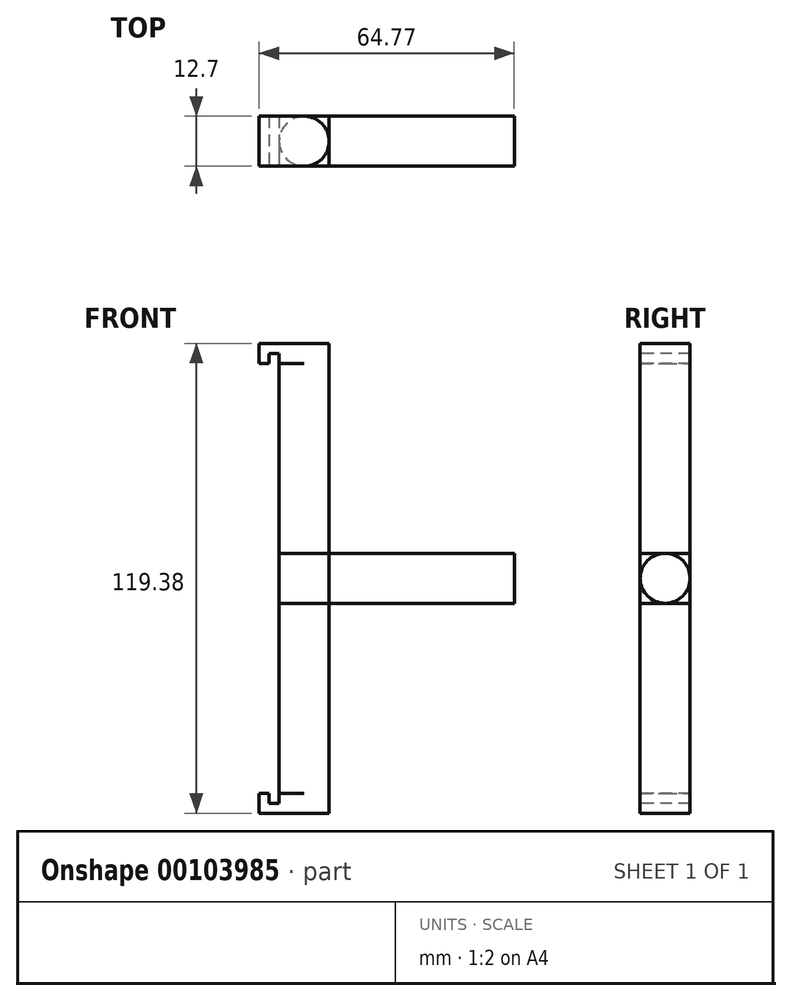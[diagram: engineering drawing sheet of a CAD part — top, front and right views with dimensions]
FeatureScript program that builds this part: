
annotation { "Feature Type Name" : "Feature", "Feature Type Description" : "" }
export const myFeature = defineFeature(function(context is Context, id is Id, definition is map)
    precondition{}
    {
        {
            var Q0;
            Q0=qCreatedBy(makeId("Right.planeOp"),FACE);
            var sketch = newSketch(context, id + "F0", { "sketchPlane" : qUnion([Q0])});
            skCircle(sketch, "E0", {"center": v(42.26, 52.7) * mm, "radius": 6.35 * mm});
            skSolve(sketch);
        }
        {
            var Q0;
            Q0=qSketchRegion(id+"F0",true);
            extrude(context, id + "F1", {"entities" : qUnion([Q0]), "depth" : 47 * mm});
        }
        {
            var Q0;
            Q0=makeQuery(id+"F1.opExtrude","CAP_FACE",FACE,{"disambiguationData":[OSD([sQuery(id+"F0.wireOp",EDGE,"E0")])],"isStart":true});
            var sketch = newSketch(context, id + "F2", { "sketchPlane" : qUnion([Q0])});
            skLineSegment(sketch, "E1", {"start": v(-42.26, 52.7) * mm, "end": v(-48.6, 52.7) * mm, "construction": true});
            skLineSegment(sketch, "E2", {"start": v(-42.26, 52.7) * mm, "end": v(-42.26, 59.04) * mm, "construction": true});
            skLineSegment(sketch, "E3.top", {"start": v(-48.6, 46.34) * mm, "end": v(-35.9, 46.34) * mm});
            skLineSegment(sketch, "E3.left", {"start": v(-48.6, 59.04) * mm, "end": v(-48.6, 46.34) * mm});
            skLineSegment(sketch, "E3.right", {"start": v(-35.9, 59.04) * mm, "end": v(-35.9, 46.34) * mm});
            skPoint(sketch, "E3.middle", {"position": v(-42.26, 52.7) * mm});
            skLineSegment(sketch, "E4", {"start": v(-35.9, 52.7) * mm, "end": v(-48.6, 52.7) * mm});
            skSolve(sketch);
        }
        {
            var Q0;
            {var subQ0=sQuery(id+"F2.wireOp",EDGE,"E3.left");var subQ1=sQuery(id+"F2.wireOp",EDGE,"E3.bottom");var subQ2=makeQuery(id+"F2.imprint","INTERSECT",VERTEX,{"derivedFrom":[subQ1,subQ0]});Q0=makeQuery(id+"F2.imprint","IMPRINT",FACE,{"disambiguationData":[TD([[makeQuery(id+"F2.imprint","IMPRINT",EDGE,{"disambiguationData":[TD([[subQ2,-1.0]])],"derivedFrom":subQ1}),-1.0]])]});}
            var Q1;
            {var subQ0=sQuery(id+"F2.wireOp",EDGE,"E3.right");var subQ1=sQuery(id+"F2.wireOp",EDGE,"E3.bottom");var subQ2=makeQuery(id+"F2.imprint","INTERSECT",VERTEX,{"derivedFrom":[subQ1,subQ0]});Q1=makeQuery(id+"F2.imprint","IMPRINT",FACE,{"disambiguationData":[TD([[makeQuery(id+"F2.imprint","IMPRINT",EDGE,{"disambiguationData":[TD([[subQ2,1.0]])],"derivedFrom":subQ1}),-1.0]])]});}
            var Q2;
            {var subQ0=makeQuery(id+"F1.opExtrude","CAP_EDGE",EDGE,{"disambiguationData":[OSD([sQuery(id+"F0.wireOp",EDGE,"E0")])],"isStart":true});var subQ1=makeQuery(id+"F2.imprint","INTERSECT",VERTEX,{"derivedFrom":[subQ0,sQuery(id+"F2.wireOp",EDGE,"E3.bottom")]});Q2=makeQuery(id+"F2.imprint","IMPRINT",FACE,{"disambiguationData":[TD([[makeQuery(id+"F2.imprint","IMPRINT",EDGE,{"disambiguationData":[TD([[subQ1,1.0]])],"derivedFrom":subQ0}),-1.0]])]});}
            var Q3;
            {var subQ0=sQuery(id+"F2.wireOp",EDGE,"E3.left");var subQ1=sQuery(id+"F2.wireOp",EDGE,"E3.top");var subQ2=makeQuery(id+"F2.imprint","INTERSECT",VERTEX,{"derivedFrom":[subQ1,subQ0]});Q3=makeQuery(id+"F2.imprint","IMPRINT",FACE,{"disambiguationData":[TD([[makeQuery(id+"F2.imprint","IMPRINT",EDGE,{"disambiguationData":[TD([[subQ2,-1.0]])],"derivedFrom":subQ1}),1.0]])]});}
            var Q4;
            {var subQ0=sQuery(id+"F2.wireOp",EDGE,"E3.right");var subQ1=sQuery(id+"F2.wireOp",EDGE,"E3.top");var subQ2=makeQuery(id+"F2.imprint","INTERSECT",VERTEX,{"derivedFrom":[subQ1,subQ0]});Q4=makeQuery(id+"F2.imprint","IMPRINT",FACE,{"disambiguationData":[TD([[makeQuery(id+"F2.imprint","IMPRINT",EDGE,{"disambiguationData":[TD([[subQ2,1.0]])],"derivedFrom":subQ1}),1.0]])]});}
            extrude(context, id + "F3", {"entities" : qUnion([Q0, Q1, Q2, Q3, Q4]), "operationType" : NewBodyOperationType.ADD, "depth" : 12.7 * mm});
        }
        {
            var Q0;
            Q0=makeQuery(id+"F3.opExtrude","SWEPT_FACE",FACE,{"disambiguationData":[OSD([sQuery(id+"F2.wireOp",EDGE,"E3.top")])]});
            var sketch = newSketch(context, id + "F4", { "sketchPlane" : qUnion([Q0])});
            skCircle(sketch, "E5", {"center": v(-6.35, -42.26) * mm, "radius": 6.35 * mm});
            skPoint(sketch, "E5.centerSnap0", {"position": v(-6.35, -48.6) * mm});
            skPoint(sketch, "E5.centerSnap1", {"position": v(-12.7, -42.26) * mm});
            skSolve(sketch);
        }
        {
            var Q0;
            {var subQ0=sQuery(id+"F4.wireOp",EDGE,"E5");var subQ4=sQuery(id+"F2.wireOp",EDGE,"E3.top");var subQ10=makeQuery(id+"F4.imprint","INTERSECT",VERTEX,{"derivedFrom":[makeQuery(id+"F3.opExtrude","CAP_EDGE",EDGE,{"disambiguationData":[OSD([subQ4])],"isStart":false}),subQ0]});Q0=makeQuery(id+"F4.imprint","IMPRINT",FACE,{"disambiguationData":[TD([[makeQuery(id+"F4.imprint","IMPRINT",EDGE,{"disambiguationData":[TD([[subQ10,1.0]])],"derivedFrom":subQ0}),1.0]])]});}
            extrude(context, id + "F5", {"entities" : qUnion([Q0]), "operationType" : NewBodyOperationType.ADD, "depth" : 50.8 * mm});
        }
        {
            var Q0;
            Q0=makeQuery(id+"F5.opExtrude","CAP_FACE",FACE,{"disambiguationData":[OSD([sQuery(id+"F4.wireOp",EDGE,"E5")])],"isStart":false});
            var sketch = newSketch(context, id + "F6", { "sketchPlane" : qUnion([Q0])});
            skLineSegment(sketch, "E6", {"start": v(-6.35, -42.26) * mm, "end": v(-6.35, -48.6) * mm});
            skLineSegment(sketch, "E7", {"start": v(-6.35, -42.26) * mm, "end": v(-12.7, -42.26) * mm});
            skLineSegment(sketch, "E8", {"start": v(-6.35, -48.6) * mm, "end": v(-12.7, -48.6) * mm});
            skLineSegment(sketch, "E9", {"start": v(-6.35, -42.26) * mm, "end": v(-6.35, -35.9) * mm});
            skLineSegment(sketch, "E10", {"start": v(-6.35, -35.9) * mm, "end": v(-12.7, -35.9) * mm});
            skLineSegment(sketch, "E11", {"start": v(-12.7, -35.9) * mm, "end": v(-12.7, -42.26) * mm});
            skLineSegment(sketch, "E12", {"start": v(-12.7, -48.6) * mm, "end": v(-12.7, -42.26) * mm});
            skLineSegment(sketch, "E13", {"start": v(-12.7, -48.6) * mm, "end": v(-17.78, -48.6) * mm});
            skLineSegment(sketch, "E14", {"start": v(-17.78, -48.6) * mm, "end": v(-17.78, -35.9) * mm});
            skLineSegment(sketch, "E15", {"start": v(-17.78, -35.9) * mm, "end": v(-12.7, -35.9) * mm});
            skLineSegment(sketch, "E16", {"start": v(-15.24, -48.6) * mm, "end": v(-15.24, -35.9) * mm});
            skSolve(sketch);
        }
        {
            var Q0;
            {var subQ0=sQuery(id+"F6.wireOp",EDGE,"E6");Q0=makeQuery(id+"F6.imprint","IMPRINT",FACE,{"disambiguationData":[TD([[makeQuery(id+"F6.imprint","IMPRINT",EDGE,{"derivedFrom":subQ0}),1.0]])]});}
            var Q1;
            {var subQ0=sQuery(id+"F6.wireOp",EDGE,"E7");Q1=makeQuery(id+"F6.imprint","IMPRINT",FACE,{"disambiguationData":[TD([[makeQuery(id+"F6.imprint","IMPRINT",EDGE,{"derivedFrom":subQ0}),-1.0]])]});}
            var Q2;
            {var subQ0=sQuery(id+"F6.wireOp",EDGE,"E6");Q2=makeQuery(id+"F6.imprint","IMPRINT",FACE,{"disambiguationData":[TD([[makeQuery(id+"F6.imprint","IMPRINT",EDGE,{"derivedFrom":subQ0}),-1.0]])]});}
            var Q3;
            {var subQ0=sQuery(id+"F6.wireOp",EDGE,"E8");Q3=makeQuery(id+"F6.imprint","IMPRINT",FACE,{"disambiguationData":[TD([[makeQuery(id+"F6.imprint","IMPRINT",EDGE,{"derivedFrom":subQ0}),-1.0]])]});}
            var Q4;
            {var subQ0=sQuery(id+"F6.wireOp",EDGE,"E10");Q4=makeQuery(id+"F6.imprint","IMPRINT",FACE,{"disambiguationData":[TD([[makeQuery(id+"F6.imprint","IMPRINT",EDGE,{"derivedFrom":subQ0}),1.0]])]});}
            var Q5;
            {var subQ1=sQuery(id+"F6.wireOp",EDGE,"E11");Q5=makeQuery(id+"F6.imprint","IMPRINT",FACE,{"disambiguationData":[TD([[makeQuery(id+"F6.imprint","IMPRINT",EDGE,{"derivedFrom":subQ1}),-1.0]])]});}
            var Q6;
            {var subQ0=sQuery(id+"F6.wireOp",EDGE,"E14");Q6=makeQuery(id+"F6.imprint","IMPRINT",FACE,{"disambiguationData":[TD([[makeQuery(id+"F6.imprint","IMPRINT",EDGE,{"derivedFrom":subQ0}),-1.0]])]});}
            extrude(context, id + "F7", {"entities" : qUnion([Q0, Q1, Q2, Q3, Q4, Q5, Q6]), "operationType" : NewBodyOperationType.ADD, "depth" : 2.54 * mm});
        }
        {
            var Q0;
            {var subQ0=sQuery(id+"F6.wireOp",EDGE,"E10");Q0=makeQuery(id+"F6.imprint","IMPRINT",FACE,{"disambiguationData":[TD([[makeQuery(id+"F6.imprint","IMPRINT",EDGE,{"derivedFrom":subQ0}),1.0]])]});}
            var Q1;
            {var subQ0=sQuery(id+"F6.wireOp",EDGE,"E8");Q1=makeQuery(id+"F6.imprint","IMPRINT",FACE,{"disambiguationData":[TD([[makeQuery(id+"F6.imprint","IMPRINT",EDGE,{"derivedFrom":subQ0}),-1.0]])]});}
            var Q2;
            {var subQ0=sQuery(id+"F6.wireOp",EDGE,"E14");Q2=makeQuery(id+"F6.imprint","IMPRINT",FACE,{"disambiguationData":[TD([[makeQuery(id+"F6.imprint","IMPRINT",EDGE,{"derivedFrom":subQ0}),-1.0]])]});}
            extrude(context, id + "F8", {"entities" : qUnion([Q0, Q1, Q2]), "operationType" : NewBodyOperationType.ADD, "oppositeDirection" : true, "depth" : 2.54 * mm});
        }
        {
            var Q0;
            Q0=makeQuery(id+"F1.opExtrude","SWEPT_BODY",BODY,{"disambiguationData":[OSD([sQuery(id+"F0.wireOp",EDGE,"E0")])]});
            var Q1;
            Q1=makeQuery(id+"F3.opExtrude","SWEPT_FACE",FACE,{"disambiguationData":[OSD([sQuery(id+"F2.wireOp",EDGE,"E4")])]});
            mirror(context, id + "F9", {"operationType" : NewBodyOperationType.ADD, "entities" : qUnion([Q0]), "mirrorPlane" : qUnion([Q1])});
        }
    });
